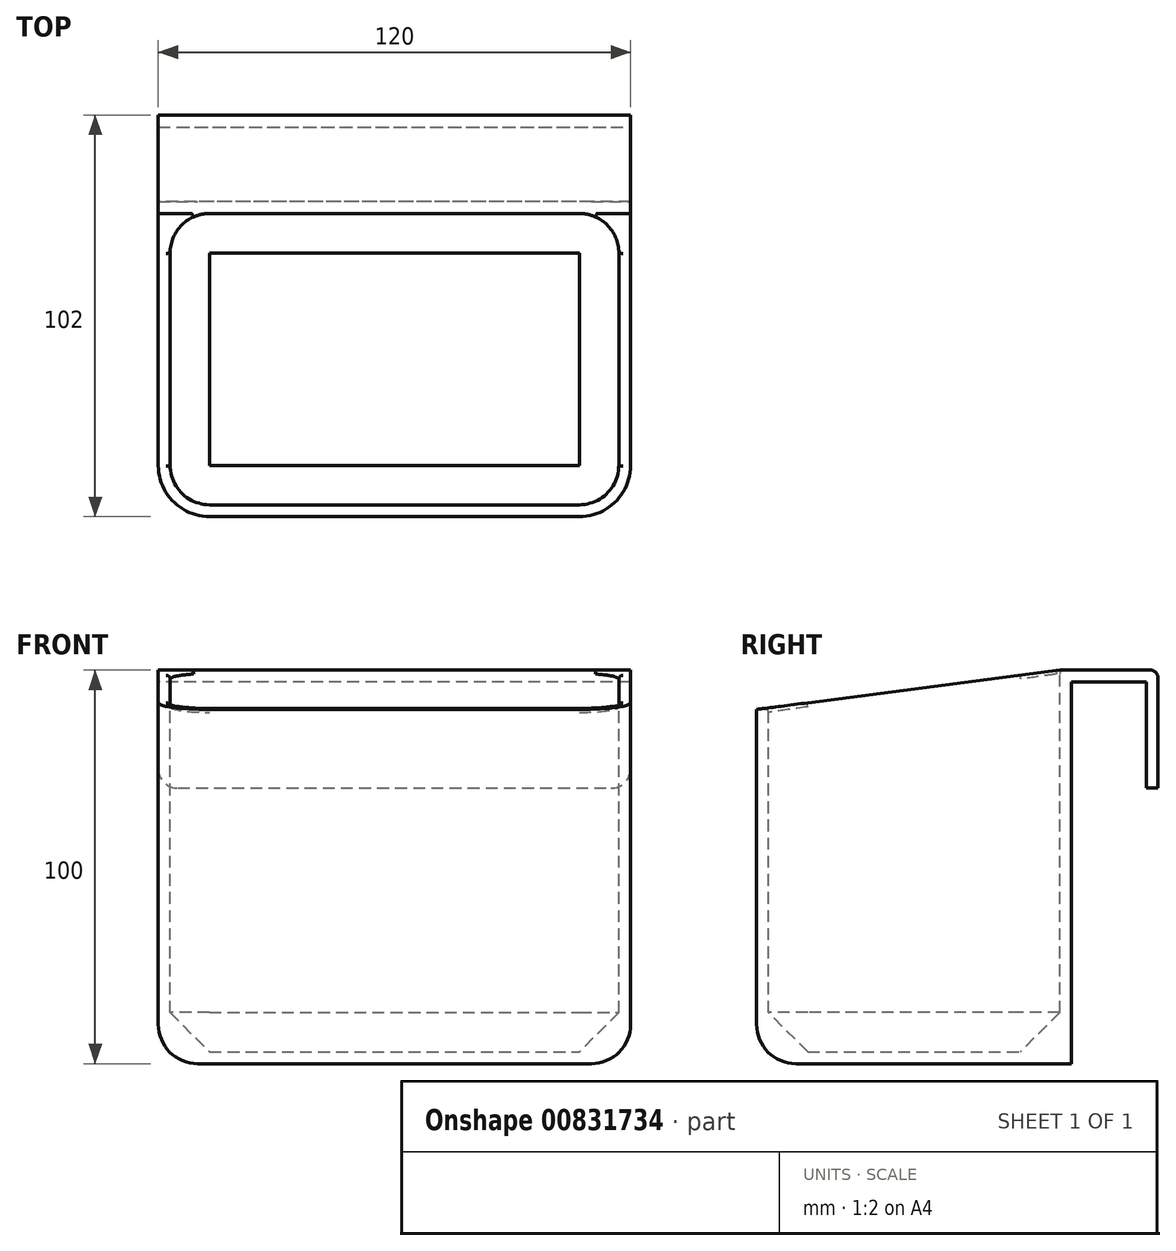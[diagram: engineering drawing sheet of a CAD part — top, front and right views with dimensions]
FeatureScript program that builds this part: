
annotation { "Feature Type Name" : "Feature", "Feature Type Description" : "" }
export const myFeature = defineFeature(function(context is Context, id is Id, definition is map)
    precondition{}
    {
        {
            var Q0;
            Q0=qCreatedBy(makeId("Top.planeOp"),FACE);
            var sketch = newSketch(context, id + "F0", { "sketchPlane" : qUnion([Q0])});
            skLineSegment(sketch, "E0.bottom", {"start": v(60, 40) * mm, "end": v(-60, 40) * mm});
            skLineSegment(sketch, "E0.top", {"start": v(60, -40) * mm, "end": v(-60, -40) * mm});
            skLineSegment(sketch, "E0.left", {"start": v(60, 40) * mm, "end": v(60, -40) * mm});
            skLineSegment(sketch, "E0.right", {"start": v(-60, 40) * mm, "end": v(-60, -40) * mm});
            skPoint(sketch, "E0.middle", {"position": v(0, 0) * mm});
            skLineSegment(sketch, "E1", {"start": v(-60, 40) * mm, "end": v(-60, 59) * mm});
            skLineSegment(sketch, "E2", {"start": v(60, 40) * mm, "end": v(60, 59) * mm});
            skLineSegment(sketch, "E3", {"start": v(-60, 59) * mm, "end": v(60, 59) * mm});
            skLineSegment(sketch, "E4", {"start": v(-60, 59) * mm, "end": v(-60, 61) * mm});
            skLineSegment(sketch, "E5", {"start": v(60, 59) * mm, "end": v(60, 61) * mm});
            skLineSegment(sketch, "E6", {"start": v(60, 61) * mm, "end": v(-60, 61) * mm});
            skSolve(sketch);
        }
        {
            var Q0;
            Q0=makeQuery(id+"F0.imprint","IMPRINT",FACE,{"disambiguationData":[TD([[makeQuery(id+"F0.imprint","IMPRINT",EDGE,{"derivedFrom":sQuery(id+"F0.wireOp",EDGE,"E0.bottom")}),1.0]])]});
            extrude(context, id + "F1", {"entities" : qUnion([Q0]), "depth" : 100 * mm, "offsetDistance" : 25 * mm});
        }
        {
            var Q0;
            Q0=makeQuery(id+"F1.opExtrude","CAP_FACE",FACE,{"disambiguationData":[OSD([sQuery(id+"F0.wireOp",EDGE,"E0.bottom"),sQuery(id+"F0.wireOp",EDGE,"E0.top"),sQuery(id+"F0.wireOp",EDGE,"E0.left"),sQuery(id+"F0.wireOp",EDGE,"E0.right")])],"isStart":false});
            var sketch = newSketch(context, id + "F2", { "sketchPlane" : qUnion([Q0])});
            skLineSegment(sketch, "E7", {"start": v(60, 40) * mm, "end": v(60, 59) * mm});
            skLineSegment(sketch, "E8", {"start": v(-60, 40) * mm, "end": v(-60, 59) * mm});
            skLineSegment(sketch, "E9", {"start": v(-60, 59) * mm, "end": v(60, 59) * mm});
            skLineSegment(sketch, "E10", {"start": v(-60, 59) * mm, "end": v(-60, 62) * mm});
            skLineSegment(sketch, "E11", {"start": v(60, 59) * mm, "end": v(60, 62) * mm});
            skLineSegment(sketch, "E12", {"start": v(-60, 62) * mm, "end": v(60, 62) * mm});
            skSolve(sketch);
        }
        {
            var Q0;
            Q0=makeQuery(id+"F2.imprint","IMPRINT",FACE,{"disambiguationData":[TD([[makeQuery(id+"F2.imprint","IMPRINT",EDGE,{"derivedFrom":sQuery(id+"F2.wireOp",EDGE,"E7")}),1.0]])]});
            extrude(context, id + "F3", {"entities" : qUnion([Q0]), "operationType" : NewBodyOperationType.ADD, "depth" : -3 * mm, "offsetDistance" : 25 * mm});
        }
        {
            var Q0;
            Q0=qSketchRegion(id+"F2",true);
            var Q1;
            Q1=makeQuery(id+"F2.imprint","IMPRINT",FACE,{"disambiguationData":[TD([[makeQuery(id+"F2.imprint","IMPRINT",EDGE,{"derivedFrom":sQuery(id+"F2.wireOp",EDGE,"E9")}),1.0]])]});
            extrude(context, id + "F4", {"entities" : qUnion([Q0, Q1]), "operationType" : NewBodyOperationType.ADD, "depth" : -30 * mm, "offsetDistance" : 25 * mm});
        }
        {
            var Q0;
            Q0=makeQuery(id+"F2.imprint","IMPRINT",FACE,{"disambiguationData":[TD([[makeQuery(id+"F2.imprint","IMPRINT",EDGE,{"derivedFrom":makeQuery(id+"F1.opExtrude","CAP_EDGE",EDGE,{"disambiguationData":[OSD([sQuery(id+"F0.wireOp",EDGE,"E0.bottom")])],"isStart":false})}),1.0]])]});
            var sketch = newSketch(context, id + "F5", { "sketchPlane" : qUnion([Q0])});
            skLineSegment(sketch, "E13.bottom", {"start": v(57, 37) * mm, "end": v(-57, 37) * mm});
            skLineSegment(sketch, "E13.top", {"start": v(57, -37) * mm, "end": v(-57, -37) * mm});
            skLineSegment(sketch, "E13.left", {"start": v(57, 37) * mm, "end": v(57, -37) * mm});
            skLineSegment(sketch, "E13.right", {"start": v(-57, 37) * mm, "end": v(-57, -37) * mm});
            skPoint(sketch, "E13.middle", {"position": v(0, 0) * mm});
            skSolve(sketch);
        }
        {
            var Q0;
            Q0=makeQuery(id+"F5.imprint","IMPRINT",FACE,{"disambiguationData":[TD([[makeQuery(id+"F5.imprint","IMPRINT",EDGE,{"derivedFrom":sQuery(id+"F5.wireOp",EDGE,"E13.bottom")}),1.0]])]});
            extrude(context, id + "F6", {"entities" : qUnion([Q0]), "operationType" : NewBodyOperationType.REMOVE, "oppositeDirection" : true, "depth" : 97 * mm, "offsetDistance" : 25 * mm});
        }
        {
            var Q0;
            Q0=makeQuery(id+"F4.boolean.opBoolean","MERGE",FACE,{"derivedFrom":[makeQuery(id+"F3.boolean.opBoolean","MERGE",FACE,{"derivedFrom":[makeQuery(id+"F1.opExtrude","SWEPT_FACE",FACE,{"disambiguationData":[OSD([sQuery(id+"F0.wireOp",EDGE,"E0.left")])]}),makeQuery(id+"F3.opExtrude","SWEPT_FACE",FACE,{"disambiguationData":[OSD([sQuery(id+"F2.wireOp",EDGE,"E7")])]})]}),makeQuery(id+"F4.opExtrude","SWEPT_FACE",FACE,{"disambiguationData":[OSD([sQuery(id+"F2.wireOp",EDGE,"E11")])]})]});
            var sketch = newSketch(context, id + "F7", { "sketchPlane" : qUnion([Q0])});
            skLineSegment(sketch, "E14", {"start": v(-40, 100) * mm, "end": v(-40, 90) * mm});
            skLineSegment(sketch, "E15", {"start": v(-40, 90) * mm, "end": v(37, 100) * mm});
            skLineSegment(sketch, "E16", {"start": v(37, 100) * mm, "end": v(-40, 100) * mm});
            skSolve(sketch);
        }
        {
            var Q0;
            Q0=makeQuery(id+"F7.imprint","IMPRINT",FACE,{"disambiguationData":[TD([[makeQuery(id+"F7.imprint","IMPRINT",EDGE,{"derivedFrom":sQuery(id+"F7.wireOp",EDGE,"E14")}),1.0]])]});
            extrude(context, id + "F8", {"entities" : qUnion([Q0]), "operationType" : NewBodyOperationType.REMOVE, "oppositeDirection" : true, "depth" : 120 * mm, "offsetDistance" : 25 * mm});
        }
        {
            var Q0;
            Q0=makeQuery(id+"F6.boolean.opBoolean","COPY",EDGE,{"derivedFrom":makeQuery(id+"F6.opExtrude","SWEPT_EDGE",EDGE,{"disambiguationData":[OSD([sQuery(id+"F5.wireOp",EDGE,"E13.bottom"),sQuery(id+"F5.wireOp",EDGE,"E13.left")])]})});
            var Q1;
            Q1=makeQuery(id+"F6.boolean.opBoolean","COPY",EDGE,{"derivedFrom":makeQuery(id+"F6.opExtrude","SWEPT_EDGE",EDGE,{"disambiguationData":[OSD([sQuery(id+"F5.wireOp",EDGE,"E13.top"),sQuery(id+"F5.wireOp",EDGE,"E13.left")])]})});
            var Q2;
            Q2=makeQuery(id+"F6.boolean.opBoolean","COPY",EDGE,{"derivedFrom":makeQuery(id+"F6.opExtrude","SWEPT_EDGE",EDGE,{"disambiguationData":[OSD([sQuery(id+"F5.wireOp",EDGE,"E13.top"),sQuery(id+"F5.wireOp",EDGE,"E13.right")])]})});
            var Q3;
            Q3=makeQuery(id+"F6.boolean.opBoolean","COPY",EDGE,{"derivedFrom":makeQuery(id+"F6.opExtrude","SWEPT_EDGE",EDGE,{"disambiguationData":[OSD([sQuery(id+"F5.wireOp",EDGE,"E13.bottom"),sQuery(id+"F5.wireOp",EDGE,"E13.right")])]})});
            fillet(context, id + "F9", {"entities" : qUnion([Q0, Q1, Q2, Q3]), "radius" : 10 * mm, "tangentPropagation" : true, "allowEdgeOverflow" : false});
        }
        {
            var Q0;
            Q0=makeQuery(id+"F6.boolean.opBoolean","COPY",EDGE,{"derivedFrom":makeQuery(id+"F6.opExtrude","CAP_EDGE",EDGE,{"disambiguationData":[OSD([sQuery(id+"F5.wireOp",EDGE,"E13.right")])],"isStart":false})});
            chamfer(context, id + "F10", {"entities" : qUnion([Q0]), "width" : 10 * mm, "tangentPropagation" : true});
        }
        {
            var Q0;
            Q0=makeQuery(id+"F1.opExtrude","SWEPT_EDGE",EDGE,{"disambiguationData":[OSD([sQuery(id+"F0.wireOp",EDGE,"E0.top"),sQuery(id+"F0.wireOp",EDGE,"E0.right")])]});
            var Q1;
            Q1=makeQuery(id+"F1.opExtrude","SWEPT_EDGE",EDGE,{"disambiguationData":[OSD([sQuery(id+"F0.wireOp",EDGE,"E0.top"),sQuery(id+"F0.wireOp",EDGE,"E0.left")])]});
            fillet(context, id + "F11", {"entities" : qUnion([Q0, Q1]), "radius" : 13 * mm, "tangentPropagation" : true, "allowEdgeOverflow" : false});
        }
        {
            var Q0;
            Q0=makeQuery(id+"F1.opExtrude","CAP_EDGE",EDGE,{"disambiguationData":[OSD([sQuery(id+"F0.wireOp",EDGE,"E0.top")])],"isStart":true});
            fillet(context, id + "F12", {"entities" : qUnion([Q0]), "radius" : 10 * mm, "tangentPropagation" : true, "allowEdgeOverflow" : false});
        }
        {
            var Q0;
            Q0=makeQuery(id+"F4.opExtrude","CAP_EDGE",EDGE,{"disambiguationData":[OSD([sQuery(id+"F2.wireOp",EDGE,"E11")])],"isStart":false});
            var Q1;
            Q1=makeQuery(id+"F4.opExtrude","CAP_EDGE",EDGE,{"disambiguationData":[OSD([sQuery(id+"F2.wireOp",EDGE,"E10")])],"isStart":false});
            fillet(context, id + "F13", {"entities" : qUnion([Q0, Q1]), "radius" : 5 * mm, "tangentPropagation" : true, "allowEdgeOverflow" : false});
        }
        {
            var Q0;
            Q0=makeQuery(id+"F4.opExtrude","CAP_EDGE",EDGE,{"disambiguationData":[OSD([sQuery(id+"F2.wireOp",EDGE,"E12")])],"isStart":true});
            fillet(context, id + "F14", {"entities" : qUnion([Q0]), "radius" : 2 * mm, "tangentPropagation" : true, "allowEdgeOverflow" : false});
        }
        {
            var Q0;
            Q0=makeQuery(id+"F8.boolean.opBoolean","INTERSECT",EDGE,{"derivedFrom":[makeQuery(id+"F6.boolean.opBoolean","COPY",FACE,{"derivedFrom":makeQuery(id+"F6.opExtrude","SWEPT_FACE",FACE,{"disambiguationData":[OSD([sQuery(id+"F5.wireOp",EDGE,"E13.left")])]})}),makeQuery(id+"F8.opExtrude","SWEPT_FACE",FACE,{"disambiguationData":[OSD([sQuery(id+"F7.wireOp",EDGE,"E15")])]})]});
            var Q1;
            Q1=makeQuery(id+"F6.boolean.opBoolean","COPY",EDGE,{"derivedFrom":makeQuery(id+"F6.opExtrude","CAP_EDGE",EDGE,{"disambiguationData":[OSD([sQuery(id+"F5.wireOp",EDGE,"E13.bottom")])],"isStart":true})});
            var Q2;
            Q2=makeQuery(id+"F8.boolean.opBoolean","INTERSECT",EDGE,{"derivedFrom":[makeQuery(id+"F6.boolean.opBoolean","COPY",FACE,{"derivedFrom":makeQuery(id+"F6.opExtrude","SWEPT_FACE",FACE,{"disambiguationData":[OSD([sQuery(id+"F5.wireOp",EDGE,"E13.right")])]})}),makeQuery(id+"F8.opExtrude","SWEPT_FACE",FACE,{"disambiguationData":[OSD([sQuery(id+"F7.wireOp",EDGE,"E15")])]})]});
            var Q3;
            Q3=makeQuery(id+"F8.boolean.opBoolean","INTERSECT",EDGE,{"derivedFrom":[makeQuery(id+"F6.boolean.opBoolean","COPY",FACE,{"derivedFrom":makeQuery(id+"F6.opExtrude","SWEPT_FACE",FACE,{"disambiguationData":[OSD([sQuery(id+"F5.wireOp",EDGE,"E13.top")])]})}),makeQuery(id+"F8.opExtrude","SWEPT_FACE",FACE,{"disambiguationData":[OSD([sQuery(id+"F7.wireOp",EDGE,"E15")])]})]});
            var Q4;
            Q4=makeQuery(id+"F9.opFillet","BLEND_EDGE",EDGE,{"blendedFrom":[makeQuery(id+"F6.boolean.opBoolean","COPY",EDGE,{"derivedFrom":makeQuery(id+"F6.opExtrude","SWEPT_EDGE",EDGE,{"disambiguationData":[OSD([sQuery(id+"F5.wireOp",EDGE,"E13.bottom"),sQuery(id+"F5.wireOp",EDGE,"E13.left")])]})}),makeQuery(id+"F8.boolean.opBoolean","COPY",FACE,{"derivedFrom":makeQuery(id+"F8.opExtrude","SWEPT_FACE",FACE,{"disambiguationData":[OSD([sQuery(id+"F7.wireOp",EDGE,"E15")])]})})],"blendedInto":[makeQuery(id+"F8.boolean.opBoolean","COPY",FACE,{"derivedFrom":makeQuery(id+"F8.opExtrude","SWEPT_FACE",FACE,{"disambiguationData":[OSD([sQuery(id+"F7.wireOp",EDGE,"E15")])]})})]});
            var Q5;
            Q5=makeQuery(id+"F9.opFillet","BLEND_EDGE",EDGE,{"blendedFrom":[makeQuery(id+"F6.boolean.opBoolean","COPY",EDGE,{"derivedFrom":makeQuery(id+"F6.opExtrude","SWEPT_EDGE",EDGE,{"disambiguationData":[OSD([sQuery(id+"F5.wireOp",EDGE,"E13.top"),sQuery(id+"F5.wireOp",EDGE,"E13.right")])]})}),makeQuery(id+"F8.boolean.opBoolean","COPY",FACE,{"derivedFrom":makeQuery(id+"F8.opExtrude","SWEPT_FACE",FACE,{"disambiguationData":[OSD([sQuery(id+"F7.wireOp",EDGE,"E15")])]})})],"blendedInto":[makeQuery(id+"F8.boolean.opBoolean","COPY",FACE,{"derivedFrom":makeQuery(id+"F8.opExtrude","SWEPT_FACE",FACE,{"disambiguationData":[OSD([sQuery(id+"F7.wireOp",EDGE,"E15")])]})})]});
            var Q6;
            Q6=makeQuery(id+"F9.opFillet","BLEND_EDGE",EDGE,{"blendedFrom":[makeQuery(id+"F6.boolean.opBoolean","COPY",EDGE,{"derivedFrom":makeQuery(id+"F6.opExtrude","SWEPT_EDGE",EDGE,{"disambiguationData":[OSD([sQuery(id+"F5.wireOp",EDGE,"E13.top"),sQuery(id+"F5.wireOp",EDGE,"E13.left")])]})}),makeQuery(id+"F8.boolean.opBoolean","COPY",FACE,{"derivedFrom":makeQuery(id+"F8.opExtrude","SWEPT_FACE",FACE,{"disambiguationData":[OSD([sQuery(id+"F7.wireOp",EDGE,"E15")])]})})],"blendedInto":[makeQuery(id+"F8.boolean.opBoolean","COPY",FACE,{"derivedFrom":makeQuery(id+"F8.opExtrude","SWEPT_FACE",FACE,{"disambiguationData":[OSD([sQuery(id+"F7.wireOp",EDGE,"E15")])]})})]});
            var Q7;
            Q7=makeQuery(id+"F9.opFillet","BLEND_EDGE",EDGE,{"blendedFrom":[makeQuery(id+"F6.boolean.opBoolean","COPY",EDGE,{"derivedFrom":makeQuery(id+"F6.opExtrude","SWEPT_EDGE",EDGE,{"disambiguationData":[OSD([sQuery(id+"F5.wireOp",EDGE,"E13.bottom"),sQuery(id+"F5.wireOp",EDGE,"E13.right")])]})}),makeQuery(id+"F8.boolean.opBoolean","COPY",FACE,{"derivedFrom":makeQuery(id+"F8.opExtrude","SWEPT_FACE",FACE,{"disambiguationData":[OSD([sQuery(id+"F7.wireOp",EDGE,"E15")])]})})],"blendedInto":[makeQuery(id+"F8.boolean.opBoolean","COPY",FACE,{"derivedFrom":makeQuery(id+"F8.opExtrude","SWEPT_FACE",FACE,{"disambiguationData":[OSD([sQuery(id+"F7.wireOp",EDGE,"E15")])]})})]});
            fillet(context, id + "F15", {"entities" : qUnion([Q0, Q1, Q2, Q3, Q4, Q5, Q6, Q7]), "radius" : 1 * mm, "tangentPropagation" : true, "allowEdgeOverflow" : false});
        }
    });
